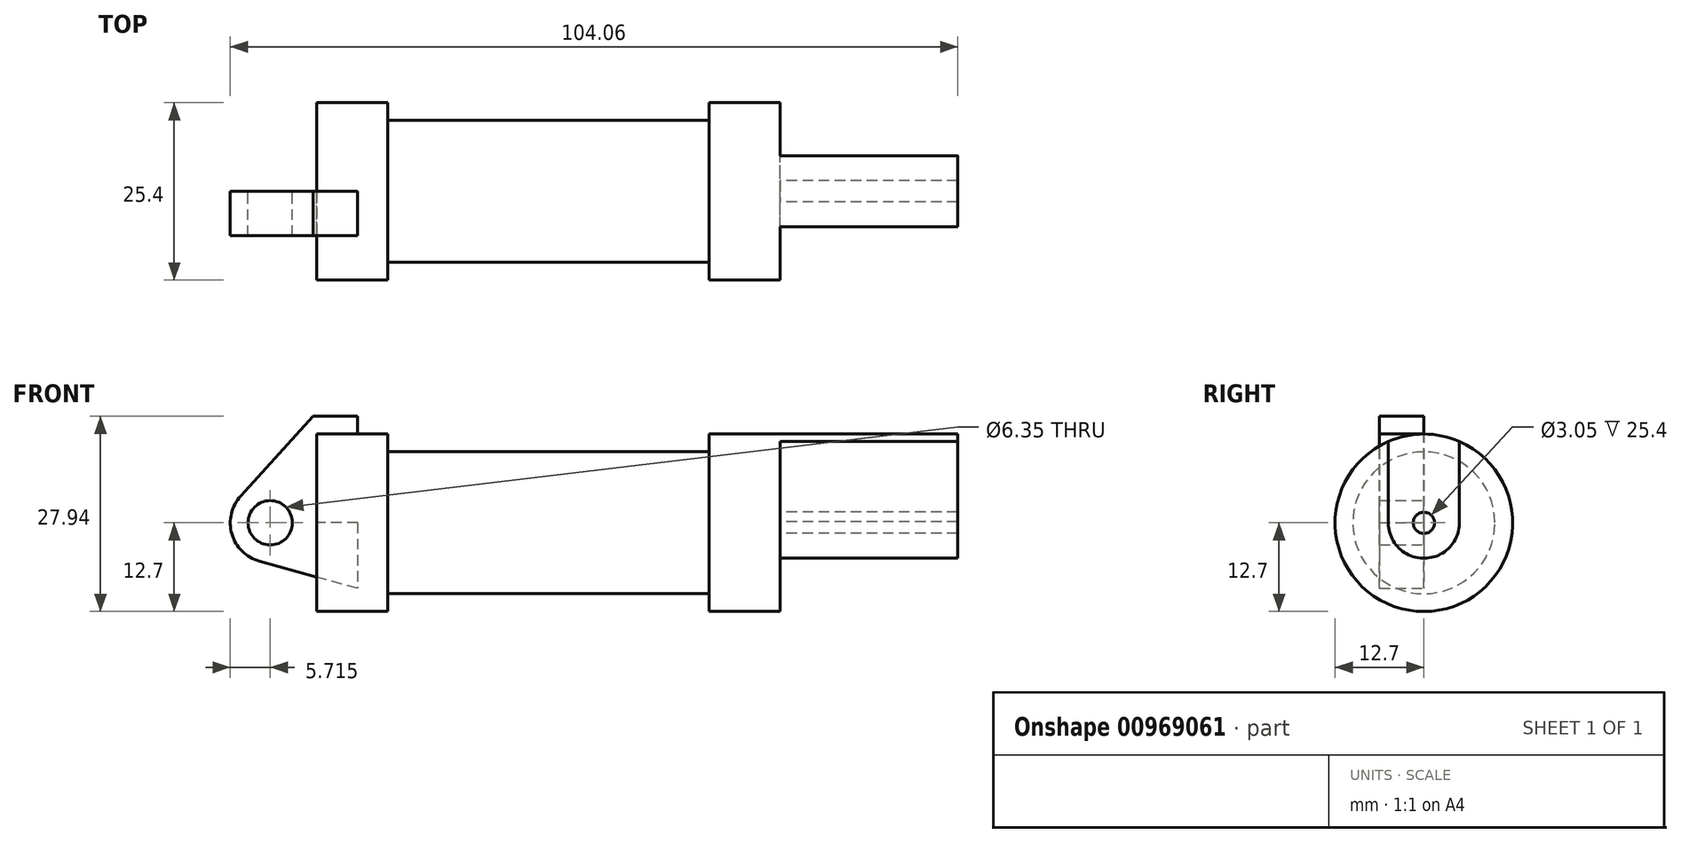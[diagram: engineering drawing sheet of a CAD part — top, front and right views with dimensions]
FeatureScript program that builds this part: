
annotation { "Feature Type Name" : "Feature", "Feature Type Description" : "" }
export const myFeature = defineFeature(function(context is Context, id is Id, definition is map)
    precondition{}
    {
        {
            var Q0;
            Q0=qCreatedBy(makeId("Front.planeOp"),FACE);
            var sketch = newSketch(context, id + "F0", { "sketchPlane" : qUnion([Q0])});
            skLineSegment(sketch, "E0", {"start": v(0, 0) * mm, "end": v(0, 12.7) * mm});
            skLineSegment(sketch, "E1", {"start": v(0, 12.7) * mm, "end": v(10.16, 12.7) * mm});
            skLineSegment(sketch, "E2", {"start": v(10.16, 12.7) * mm, "end": v(10.16, 10.16) * mm});
            skLineSegment(sketch, "E3", {"start": v(10.16, 10.16) * mm, "end": v(56.13, 10.16) * mm});
            skLineSegment(sketch, "E4", {"start": v(56.13, 10.16) * mm, "end": v(56.13, 12.7) * mm});
            skLineSegment(sketch, "E5", {"start": v(56.13, 12.7) * mm, "end": v(66.3, 12.7) * mm});
            skLineSegment(sketch, "E6", {"start": v(66.3, 12.7) * mm, "end": v(66.3, 0) * mm});
            skLineSegment(sketch, "E7", {"start": v(66.3, 0) * mm, "end": v(0, 0) * mm});
            skLineSegment(sketch, "E8", {"start": v(5.84, 15.24) * mm, "end": v(-0.5, 15.24) * mm});
            skLineSegment(sketch, "E9", {"start": v(-0.5, 15.24) * mm, "end": v(-10.88, 3.85) * mm});
            skLineSegment(sketch, "E10", {"start": v(0, 0) * mm, "end": v(-6.65, 0) * mm});
            skCircle(sketch, "E11", {"center": v(-6.65, 0) * mm, "radius": 5.72 * mm});
            skCircle(sketch, "E12", {"center": v(-6.65, 0) * mm, "radius": 3.18 * mm});
            skLineSegment(sketch, "E13", {"start": v(5.84, 15.24) * mm, "end": v(5.84, -9.4) * mm});
            skLineSegment(sketch, "E14", {"start": v(5.84, -9.4) * mm, "end": v(-8.18, -5.5) * mm});
            skSolve(sketch);
        }
        {
            var Q0;
            {var subQ0=sQuery(id+"F0.wireOp",EDGE,"E2");Q0=makeQuery(id+"F0.imprint","IMPRINT",FACE,{"disambiguationData":[TD([[makeQuery(id+"F0.imprint","IMPRINT",EDGE,{"derivedFrom":subQ0}),-1.0]])]});}
            var Q1;
            {var subQ0=sQuery(id+"F0.wireOp",EDGE,"E0");Q1=makeQuery(id+"F0.imprint","IMPRINT",FACE,{"disambiguationData":[TD([[makeQuery(id+"F0.imprint","IMPRINT",EDGE,{"derivedFrom":subQ0}),-1.0]])]});}
            var Q2;
            Q2=sQuery(id+"F0.wireOp",EDGE,"E7");
            revolve(context, id + "F1", {"surfaceOperationType" : NewSurfaceOperationType.NEW, "entities" : qUnion([Q0, Q1]), "axis" : qUnion([Q2]), "revolveType" : RevolveType.FULL});
        }
        {
            var Q0;
            {var subQ1=sQuery(id+"F0.wireOp",EDGE,"E0");Q0=makeQuery(id+"F0.imprint","IMPRINT",FACE,{"disambiguationData":[TD([[makeQuery(id+"F0.imprint","IMPRINT",EDGE,{"derivedFrom":subQ1}),1.0]])]});}
            var Q1;
            {var subQ5=sQuery(id+"F0.wireOp",EDGE,"E12");Q1=makeQuery(id+"F0.imprint","IMPRINT",FACE,{"disambiguationData":[TD([[makeQuery(id+"F0.imprint","IMPRINT",EDGE,{"derivedFrom":subQ5}),-1.0]])]});}
            var Q2;
            {var subQ0=sQuery(id+"F0.wireOp",EDGE,"E14");Q2=makeQuery(id+"F0.imprint","IMPRINT",FACE,{"disambiguationData":[TD([[makeQuery(id+"F0.imprint","IMPRINT",EDGE,{"derivedFrom":subQ0}),-1.0]])]});}
            extrude(context, id + "F2", {"entities" : qUnion([Q0, Q1, Q2]), "depth" : 6.35 * mm, "offsetDistance" : 25.4 * mm});
        }
        {
            var Q0;
            Q0=makeQuery(id+"F1.opRevolve","SWEPT_FACE",FACE,{"disambiguationData":[OSD([sQuery(id+"F0.wireOp",EDGE,"E6")])]});
            var sketch = newSketch(context, id + "F3", { "sketchPlane" : qUnion([Q0])});
            skCircle(sketch, "E15", {"center": v(0, 0) * mm, "radius": 5.08 * mm});
            skCircle(sketch, "E16", {"center": v(0, 0) * mm, "radius": 1.52 * mm});
            skLineSegment(sketch, "E17", {"start": v(-5.08, -0.05) * mm, "end": v(-5.08, 15.2) * mm});
            skLineSegment(sketch, "E18", {"start": v(5.08, 0.19) * mm, "end": v(5.08, 15.43) * mm});
            skSolve(sketch);
        }
        {
            var Q0;
            Q0=makeQuery(id+"F3.imprint","IMPRINT",FACE,{"disambiguationData":[TD([[makeQuery(id+"F3.imprint","IMPRINT",EDGE,{"derivedFrom":sQuery(id+"F3.wireOp",EDGE,"E16")}),-1.0]])]});
            var Q1;
            {var subQ0=sQuery(id+"F3.wireOp",EDGE,"E17");var subQ1=sQuery(id+"F3.wireOp",EDGE,"E15");var subQ2=makeQuery(id+"F3.imprint","INTERSECT",VERTEX,{"derivedFrom":[subQ1,subQ0]});Q1=makeQuery(id+"F3.imprint","IMPRINT",FACE,{"disambiguationData":[TD([[makeQuery(id+"F3.imprint","IMPRINT",EDGE,{"disambiguationData":[TD([[subQ2,1.0]])],"derivedFrom":subQ1}),-1.0]])]});}
            extrude(context, id + "F4", {"entities" : qUnion([Q0, Q1]), "operationType" : NewBodyOperationType.ADD, "depth" : 25.4 * mm, "offsetDistance" : 25.4 * mm});
        }
    });
